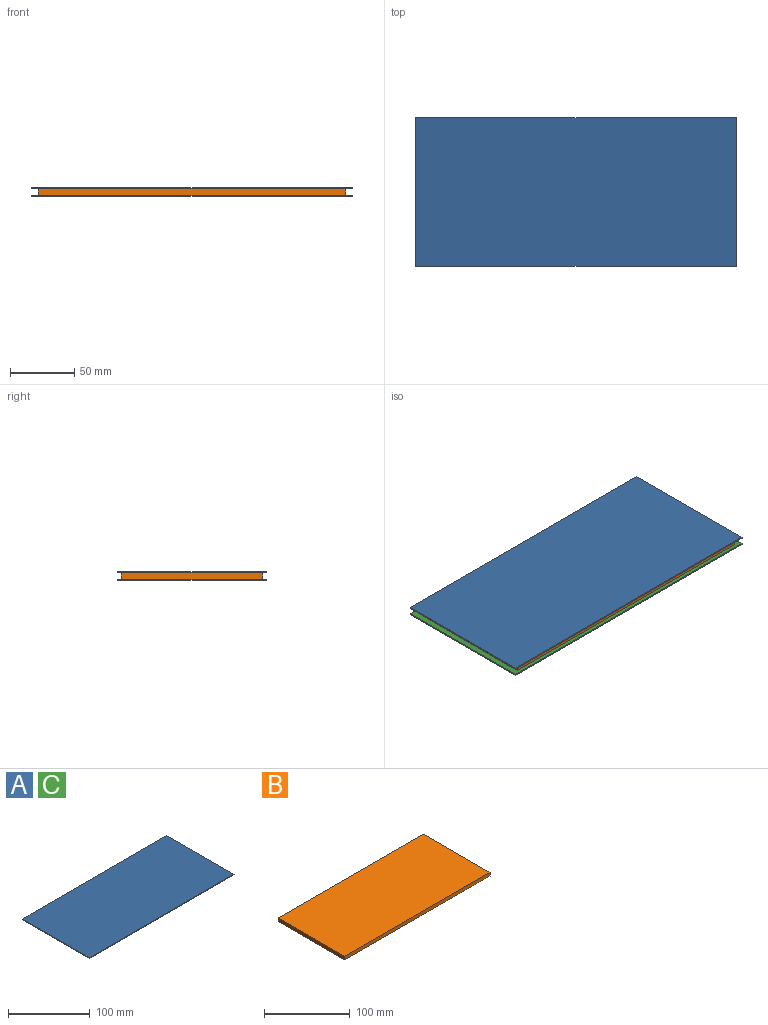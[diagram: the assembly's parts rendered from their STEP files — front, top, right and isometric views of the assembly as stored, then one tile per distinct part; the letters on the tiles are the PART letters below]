
ASSEMBLY  parts=3 mates=2
PART A: 6 faces, bbox 250x116x1 mm
  f0: plane 250x1mm, normal (0,1,0), area 250mm2, adj f1,f3,f4,f5
  f1: plane 116x1mm, normal (-1,0,0), area 116mm2, adj f0,f2,f4,f5
  f2: plane 250x1mm, normal (0,-1,0), area 250mm2, adj f1,f3,f4,f5
  f3: plane 116x1mm, normal (1,0,0), area 116mm2, adj f0,f2,f4,f5
  f4: plane 250x116mm, normal (0,0,1), area 29000mm2, adj f0,f1,f2,f3
  f5: plane 250x116mm, normal (0,0,-1), area 29000mm2, adj f0,f1,f2,f3
PART B: 6 faces, bbox 240x110x5 mm
  f0: plane 240x5mm, normal (0,1,0), area 1200mm2, adj f1,f3,f4,f5
  f1: plane 110x5mm, normal (-1,0,0), area 550mm2, adj f0,f2,f4,f5
  f2: plane 240x5mm, normal (0,-1,0), area 1200mm2, adj f1,f3,f4,f5
  f3: plane 110x5mm, normal (1,0,0), area 550mm2, adj f0,f2,f4,f5
  f4: plane 240x110mm, normal (0,0,1), area 26400mm2, adj f0,f1,f2,f3
  f5: plane 240x110mm, normal (0,0,-1), area 26400mm2, adj f0,f1,f2,f3
PART C: same geometry as A
PLACE A at identity
PLACE B rot(axis=(1,0,0),180deg) t=(0,0,0)mm
PLACE C t=(0,0,-6)mm
MATE fastened C.f4 <-> B.f4  axis (0,0,1) through (0,0,-5)mm
MATE fastened B.f5 <-> A.f5  axis (0,0,1) through (0,0,0)mm
